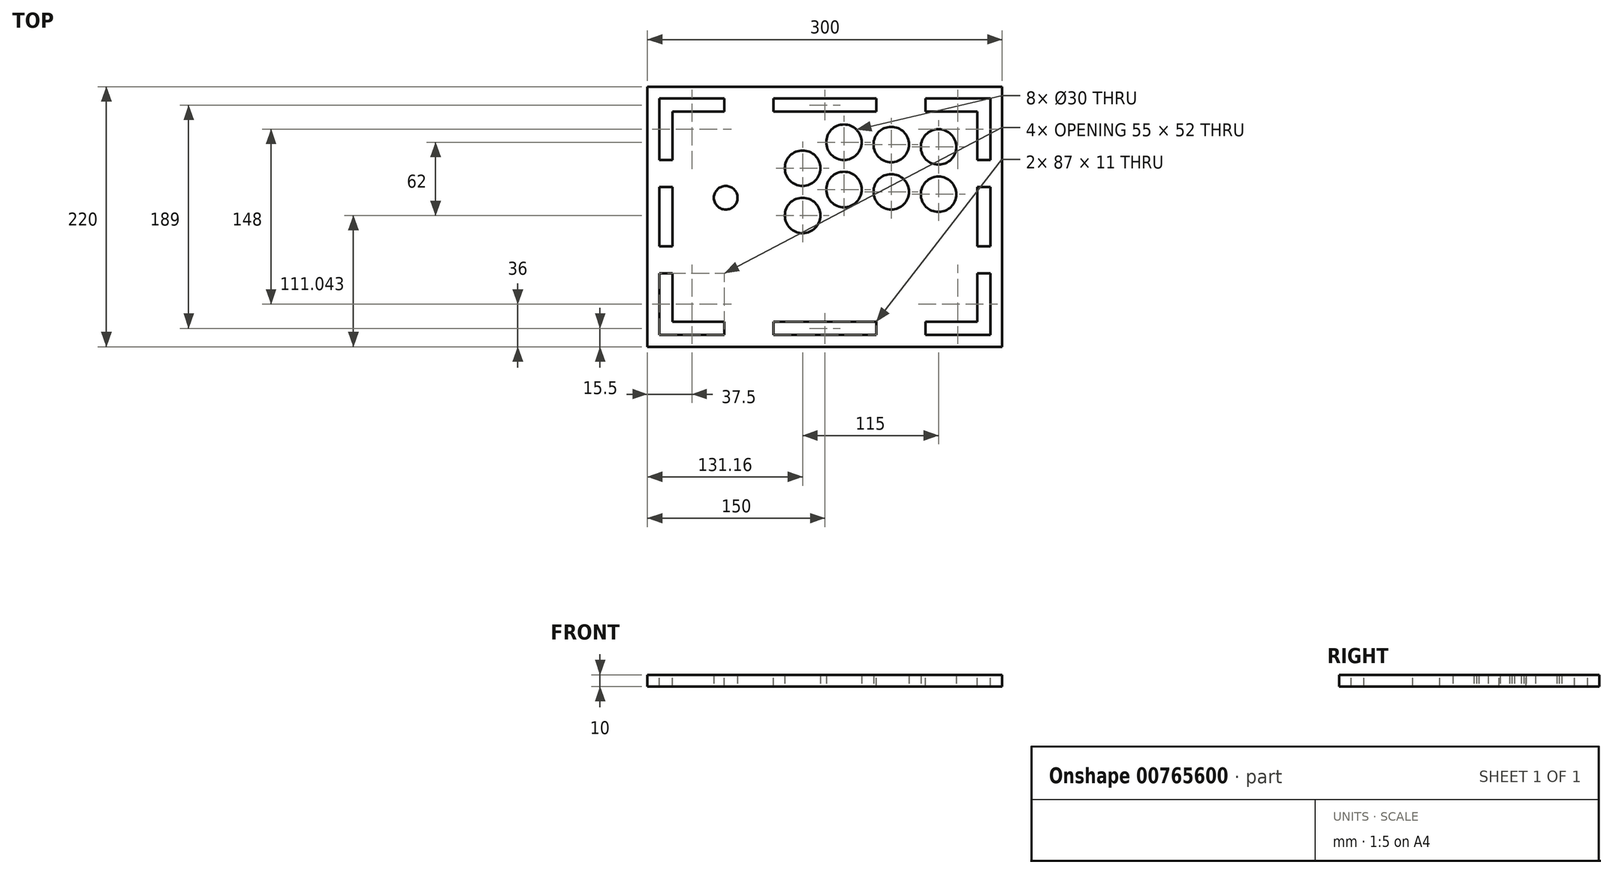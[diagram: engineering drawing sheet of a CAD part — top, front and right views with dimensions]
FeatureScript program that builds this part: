
annotation { "Feature Type Name" : "Feature", "Feature Type Description" : "" }
export const myFeature = defineFeature(function(context is Context, id is Id, definition is map)
    precondition{}
    {
        {
            var Q0;
            Q0=qCreatedBy(makeId("Top.planeOp"),FACE);
            var sketch = newSketch(context, id + "F0", { "sketchPlane" : qUnion([Q0])});
            skLineSegment(sketch, "E0.bottom", {"start": v(-150, 110) * mm, "end": v(150, 110) * mm});
            skLineSegment(sketch, "E0.top", {"start": v(-150, -110) * mm, "end": v(150, -110) * mm});
            skLineSegment(sketch, "E0.left", {"start": v(-150, 110) * mm, "end": v(-150, -110) * mm});
            skLineSegment(sketch, "E0.right", {"start": v(150, 110) * mm, "end": v(150, -110) * mm});
            skPoint(sketch, "E0.middle", {"position": v(0, 0) * mm});
            skLineSegment(sketch, "E1", {"start": v(150, -110) * mm, "end": v(-69, -110) * mm});
            skCircle(sketch, "E2", {"center": v(96.16, 19.04) * mm, "radius": 15 * mm});
            skCircle(sketch, "E3", {"center": v(96.16, 59.04) * mm, "radius": 15 * mm});
            skCircle(sketch, "E4", {"center": v(56.16, 61.04) * mm, "radius": 15 * mm});
            skCircle(sketch, "E5", {"center": v(56.16, 21.04) * mm, "radius": 15 * mm});
            skCircle(sketch, "E6", {"center": v(16.16, 23.04) * mm, "radius": 15 * mm});
            skCircle(sketch, "E7", {"center": v(16.16, 63.04) * mm, "radius": 15 * mm});
            skCircle(sketch, "E8", {"center": v(-18.84, 1.04) * mm, "radius": 15 * mm});
            skCircle(sketch, "E9", {"center": v(-18.84, 41.04) * mm, "radius": 15 * mm});
            skCircle(sketch, "E10", {"center": v(-83.84, 16.04) * mm, "radius": 10 * mm});
            skSolve(sketch);
        }
        {
            var Q0;
            Q0=makeQuery(id+"F0.imprint","IMPRINT",FACE,{"disambiguationData":[TD([[makeQuery(id+"F0.imprint","IMPRINT",EDGE,{"derivedFrom":sQuery(id+"F0.wireOp",EDGE,"E0.bottom")}),-1.0]])]});
            extrude(context, id + "F1", {"entities" : qUnion([Q0]), "depth" : 10 * mm, "offsetDistance" : 25 * mm});
        }
        {
            var Q0;
            Q0=makeQuery(id+"F1.opExtrude","CAP_FACE",FACE,{"disambiguationData":[OSD([sQuery(id+"F0.wireOp",EDGE,"E0.bottom"),sQuery(id+"F0.wireOp",EDGE,"E0.top"),sQuery(id+"F0.wireOp",EDGE,"E0.left"),sQuery(id+"F0.wireOp",EDGE,"E0.right"),sQuery(id+"F0.wireOp",EDGE,"E1"),sQuery(id+"F0.wireOp",EDGE,"E2"),sQuery(id+"F0.wireOp",EDGE,"E3"),sQuery(id+"F0.wireOp",EDGE,"E4"),sQuery(id+"F0.wireOp",EDGE,"E5"),sQuery(id+"F0.wireOp",EDGE,"E6"),sQuery(id+"F0.wireOp",EDGE,"E7"),sQuery(id+"F0.wireOp",EDGE,"E8"),sQuery(id+"F0.wireOp",EDGE,"E9"),sQuery(id+"F0.wireOp",EDGE,"E10")])],"isStart":false});
            var sketch = newSketch(context, id + "F2", { "sketchPlane" : qUnion([Q0])});
            skPoint(sketch, "E11.middle", {"position": v(0, 0) * mm});
            skLineSegment(sketch, "E12", {"start": v(140, 100) * mm, "end": v(85, 100) * mm});
            skLineSegment(sketch, "E13", {"start": v(85, 100) * mm, "end": v(85, 89) * mm});
            skLineSegment(sketch, "E14", {"start": v(85, 89) * mm, "end": v(129, 89) * mm});
            skLineSegment(sketch, "E15", {"start": v(140, 100) * mm, "end": v(140, 48) * mm});
            skLineSegment(sketch, "E16", {"start": v(140, 48) * mm, "end": v(129, 48) * mm});
            skLineSegment(sketch, "E17", {"start": v(129, 48) * mm, "end": v(129, 89) * mm});
            skLineSegment(sketch, "E18.MirrorCS", {"start": v(-140, 100) * mm, "end": v(-85, 100) * mm});
            skLineSegment(sketch, "E19.MirrorCS", {"start": v(-85, 100) * mm, "end": v(-85, 89) * mm});
            skLineSegment(sketch, "E20.MirrorCS", {"start": v(-85, 89) * mm, "end": v(-129, 89) * mm});
            skLineSegment(sketch, "E21.MirrorCS", {"start": v(-129, 48) * mm, "end": v(-129, 89) * mm});
            skLineSegment(sketch, "E22.MirrorCS", {"start": v(-140, 48) * mm, "end": v(-129, 48) * mm});
            skLineSegment(sketch, "E23.MirrorCS", {"start": v(-140, 100) * mm, "end": v(-140, 48) * mm});
            skLineSegment(sketch, "E24.MirrorCS", {"start": v(-140, -100) * mm, "end": v(-85, -100) * mm});
            skLineSegment(sketch, "E25.MirrorCS", {"start": v(-140, -100) * mm, "end": v(-140, -48) * mm});
            skLineSegment(sketch, "E26.MirrorCS", {"start": v(-140, -48) * mm, "end": v(-129, -48) * mm});
            skLineSegment(sketch, "E27.MirrorCS", {"start": v(-129, -48) * mm, "end": v(-129, -89) * mm});
            skLineSegment(sketch, "E28.MirrorCS", {"start": v(-85, -89) * mm, "end": v(-129, -89) * mm});
            skLineSegment(sketch, "E29.MirrorCS", {"start": v(-85, -100) * mm, "end": v(-85, -89) * mm});
            skLineSegment(sketch, "E30.MirrorCS", {"start": v(140, -100) * mm, "end": v(85, -100) * mm});
            skLineSegment(sketch, "E31.MirrorCS", {"start": v(85, -100) * mm, "end": v(85, -89) * mm});
            skLineSegment(sketch, "E32.MirrorCS", {"start": v(85, -89) * mm, "end": v(129, -89) * mm});
            skLineSegment(sketch, "E33.MirrorCS", {"start": v(129, -48) * mm, "end": v(129, -89) * mm});
            skLineSegment(sketch, "E34.MirrorCS", {"start": v(140, -48) * mm, "end": v(129, -48) * mm});
            skLineSegment(sketch, "E35.MirrorCS", {"start": v(140, -100) * mm, "end": v(140, -48) * mm});
            skSolve(sketch);
        }
        {
            var Q0;
            Q0=makeQuery(id+"F2.imprint","IMPRINT",FACE,{"disambiguationData":[TD([[makeQuery(id+"F2.imprint","IMPRINT",EDGE,{"derivedFrom":sQuery(id+"F2.wireOp",EDGE,"E12")}),1.0]])]});
            var Q1;
            Q1=makeQuery(id+"F2.imprint","IMPRINT",FACE,{"disambiguationData":[TD([[makeQuery(id+"F2.imprint","IMPRINT",EDGE,{"derivedFrom":sQuery(id+"F2.wireOp",EDGE,"E18.MirrorCS")}),-1.0]])]});
            var Q2;
            Q2=makeQuery(id+"F2.imprint","IMPRINT",FACE,{"disambiguationData":[TD([[makeQuery(id+"F2.imprint","IMPRINT",EDGE,{"derivedFrom":sQuery(id+"F2.wireOp",EDGE,"E25.MirrorCS")}),-1.0]])]});
            var Q3;
            Q3=makeQuery(id+"F2.imprint","IMPRINT",FACE,{"disambiguationData":[TD([[makeQuery(id+"F2.imprint","IMPRINT",EDGE,{"derivedFrom":sQuery(id+"F2.wireOp",EDGE,"E30.MirrorCS")}),-1.0]])]});
            extrude(context, id + "F3", {"entities" : qUnion([Q0, Q1, Q2, Q3]), "operationType" : NewBodyOperationType.REMOVE, "oppositeDirection" : true, "depth" : 10 * mm, "offsetDistance" : 25 * mm});
        }
        {
            var Q0;
            Q0=makeQuery(id+"F1.opExtrude","CAP_FACE",FACE,{"disambiguationData":[OSD([sQuery(id+"F0.wireOp",EDGE,"E0.bottom"),sQuery(id+"F0.wireOp",EDGE,"E0.top"),sQuery(id+"F0.wireOp",EDGE,"E0.left"),sQuery(id+"F0.wireOp",EDGE,"E0.right"),sQuery(id+"F0.wireOp",EDGE,"E1"),sQuery(id+"F0.wireOp",EDGE,"E2"),sQuery(id+"F0.wireOp",EDGE,"E3"),sQuery(id+"F0.wireOp",EDGE,"E4"),sQuery(id+"F0.wireOp",EDGE,"E5"),sQuery(id+"F0.wireOp",EDGE,"E6"),sQuery(id+"F0.wireOp",EDGE,"E7"),sQuery(id+"F0.wireOp",EDGE,"E8"),sQuery(id+"F0.wireOp",EDGE,"E9"),sQuery(id+"F0.wireOp",EDGE,"E10")])],"isStart":false});
            var sketch = newSketch(context, id + "F4", { "sketchPlane" : qUnion([Q0])});
            skLineSegment(sketch, "E36", {"start": v(-43.5, -100) * mm, "end": v(-43.5, -89) * mm});
            skLineSegment(sketch, "E37", {"start": v(-43.5, -89) * mm, "end": v(43.5, -89) * mm});
            skLineSegment(sketch, "E38", {"start": v(43.5, -89) * mm, "end": v(43.5, -100) * mm});
            skLineSegment(sketch, "E39", {"start": v(-43.5, -100) * mm, "end": v(43.5, -100) * mm});
            skLineSegment(sketch, "E40.MirrorCS", {"start": v(-43.5, 89) * mm, "end": v(43.5, 89) * mm});
            skLineSegment(sketch, "E41.MirrorCS", {"start": v(-43.5, 100) * mm, "end": v(-43.5, 89) * mm});
            skLineSegment(sketch, "E42.MirrorCS", {"start": v(-43.5, 100) * mm, "end": v(43.5, 100) * mm});
            skLineSegment(sketch, "E43.MirrorCS", {"start": v(43.5, 89) * mm, "end": v(43.5, 100) * mm});
            skSolve(sketch);
        }
        {
            var Q0;
            Q0=makeQuery(id+"F4.imprint","IMPRINT",FACE,{"disambiguationData":[TD([[makeQuery(id+"F4.imprint","IMPRINT",EDGE,{"derivedFrom":sQuery(id+"F4.wireOp",EDGE,"E40.MirrorCS")}),1.0]])]});
            var Q1;
            Q1=makeQuery(id+"F4.imprint","IMPRINT",FACE,{"disambiguationData":[TD([[makeQuery(id+"F4.imprint","IMPRINT",EDGE,{"derivedFrom":sQuery(id+"F4.wireOp",EDGE,"E36")}),-1.0]])]});
            extrude(context, id + "F5", {"entities" : qUnion([Q0, Q1]), "operationType" : NewBodyOperationType.REMOVE, "oppositeDirection" : true, "depth" : 10 * mm, "offsetDistance" : 25 * mm});
        }
        {
            var Q0;
            Q0=makeQuery(id+"F1.opExtrude","CAP_FACE",FACE,{"disambiguationData":[OSD([sQuery(id+"F0.wireOp",EDGE,"E0.bottom"),sQuery(id+"F0.wireOp",EDGE,"E0.top"),sQuery(id+"F0.wireOp",EDGE,"E0.left"),sQuery(id+"F0.wireOp",EDGE,"E0.right"),sQuery(id+"F0.wireOp",EDGE,"E1"),sQuery(id+"F0.wireOp",EDGE,"E2"),sQuery(id+"F0.wireOp",EDGE,"E3"),sQuery(id+"F0.wireOp",EDGE,"E4"),sQuery(id+"F0.wireOp",EDGE,"E5"),sQuery(id+"F0.wireOp",EDGE,"E6"),sQuery(id+"F0.wireOp",EDGE,"E7"),sQuery(id+"F0.wireOp",EDGE,"E8"),sQuery(id+"F0.wireOp",EDGE,"E9"),sQuery(id+"F0.wireOp",EDGE,"E10")])],"isStart":false});
            var sketch = newSketch(context, id + "F6", { "sketchPlane" : qUnion([Q0])});
            skLineSegment(sketch, "E44", {"start": v(140, 0) * mm, "end": v(140, -25) * mm});
            skLineSegment(sketch, "E45", {"start": v(140, -25) * mm, "end": v(140, 25) * mm});
            skLineSegment(sketch, "E46", {"start": v(140, -25) * mm, "end": v(129, -25) * mm});
            skLineSegment(sketch, "E47", {"start": v(129, 25) * mm, "end": v(140, 25) * mm});
            skLineSegment(sketch, "E48", {"start": v(129, -25) * mm, "end": v(129, 25) * mm});
            skLineSegment(sketch, "E49.MirrorCS", {"start": v(-129, -25) * mm, "end": v(-129, 25) * mm});
            skLineSegment(sketch, "E50.MirrorCS", {"start": v(-140, -25) * mm, "end": v(-129, -25) * mm});
            skLineSegment(sketch, "E51.MirrorCS", {"start": v(-140, -25) * mm, "end": v(-140, 25) * mm});
            skLineSegment(sketch, "E52.MirrorCS", {"start": v(-129, 25) * mm, "end": v(-140, 25) * mm});
            skSolve(sketch);
        }
        {
            var Q0;
            Q0=makeQuery(id+"F6.imprint","IMPRINT",FACE,{"disambiguationData":[TD([[makeQuery(id+"F6.imprint","IMPRINT",EDGE,{"derivedFrom":sQuery(id+"F6.wireOp",EDGE,"E49.MirrorCS")}),1.0]])]});
            var Q1;
            {var subQ1=sQuery(id+"F6.wireOp",EDGE,"E46");Q1=makeQuery(id+"F6.imprint","IMPRINT",FACE,{"disambiguationData":[TD([[makeQuery(id+"F6.imprint","IMPRINT",EDGE,{"derivedFrom":subQ1}),-1.0]])]});}
            extrude(context, id + "F7", {"entities" : qUnion([Q0, Q1]), "operationType" : NewBodyOperationType.REMOVE, "oppositeDirection" : true, "depth" : 10 * mm, "offsetDistance" : 25 * mm});
        }
    });
